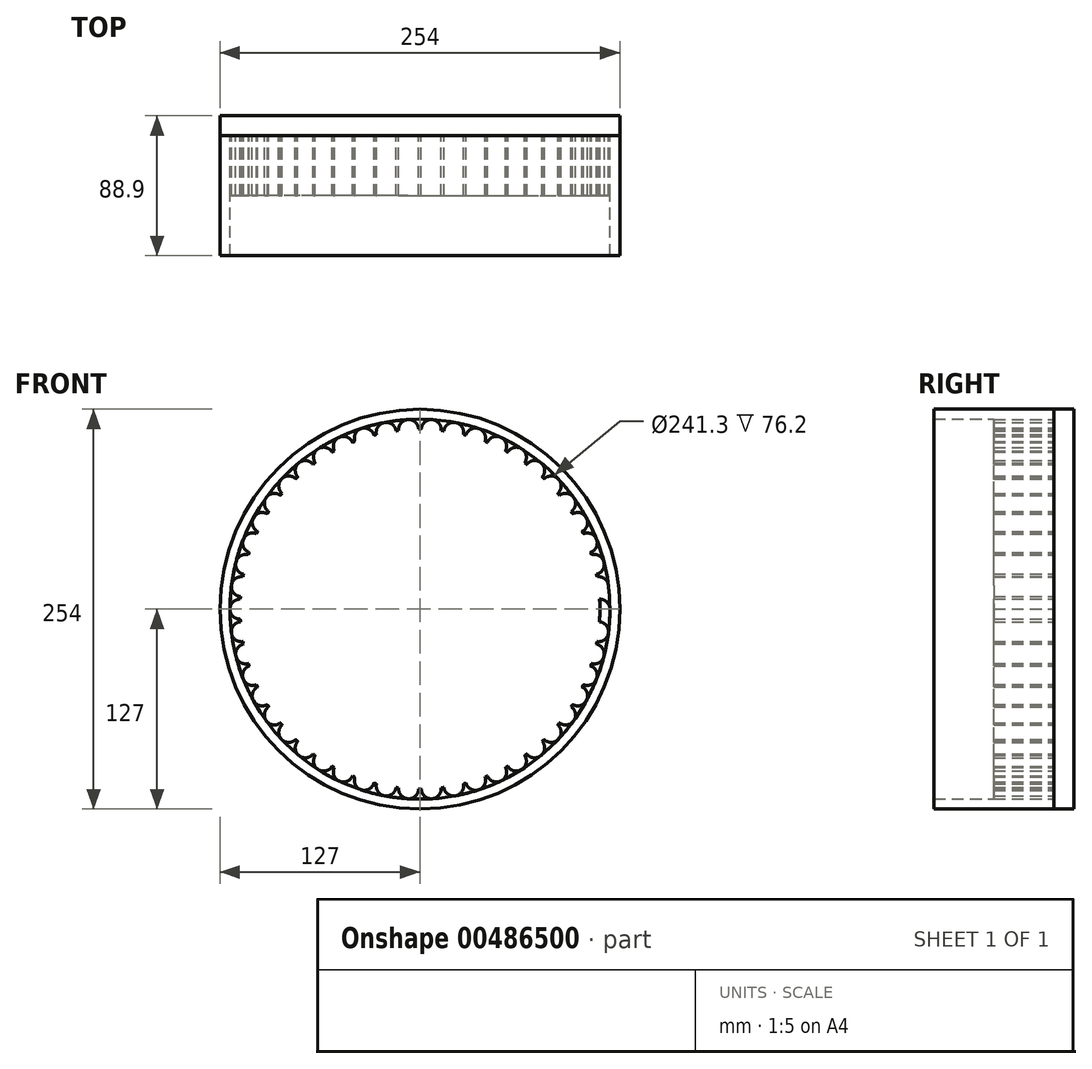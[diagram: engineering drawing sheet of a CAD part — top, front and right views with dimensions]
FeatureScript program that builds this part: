
annotation { "Feature Type Name" : "Feature", "Feature Type Description" : "" }
export const myFeature = defineFeature(function(context is Context, id is Id, definition is map)
    precondition{}
    {
        {
            var Q0;
            Q0=qCreatedBy(makeId("Front.planeOp"),FACE);
            var sketch = newSketch(context, id + "F0", { "sketchPlane" : qUnion([Q0])});
            skCircle(sketch, "E0", {"center": v(0, 0) * mm, "radius": 4.4 * mm});
            skCircle(sketch, "E1", {"center": v(0, 0) * mm, "radius": 127 * mm});
            skCircle(sketch, "E2", {"center": v(0, 0) * mm, "radius": 114.3 * mm});
            skCircle(sketch, "E3", {"center": v(0, 0) * mm, "radius": 120.65 * mm});
            skLineSegment(sketch, "E4", {"start": v(-114.3, 0) * mm, "end": v(114.3, 0) * mm});
            skLineSegment(sketch, "E5", {"start": v(0, -114.3) * mm, "end": v(0, 114.3) * mm});
            skCircle(sketch, "E6", {"center": v(-114.3, 0) * mm, "radius": 6.35 * mm});
            skCircle(sketch, "E7.1.0", {"center": v(-113.4, -14.33) * mm, "radius": 6.35 * mm});
            skCircle(sketch, "E7.2.0", {"center": v(-110.7, -28.43) * mm, "radius": 6.35 * mm});
            skCircle(sketch, "E7.3.0", {"center": v(-106.27, -42.08) * mm, "radius": 6.35 * mm});
            skCircle(sketch, "E7.4.0", {"center": v(-100.16, -55.06) * mm, "radius": 6.35 * mm});
            skCircle(sketch, "E7.5.0", {"center": v(-92.47, -67.18) * mm, "radius": 6.35 * mm});
            skCircle(sketch, "E7.6.0", {"center": v(-83.32, -78.24) * mm, "radius": 6.35 * mm});
            skCircle(sketch, "E7.7.0", {"center": v(-72.86, -88.07) * mm, "radius": 6.35 * mm});
            skCircle(sketch, "E7.8.0", {"center": v(-61.25, -96.5) * mm, "radius": 6.35 * mm});
            skCircle(sketch, "E7.9.0", {"center": v(-48.67, -103.42) * mm, "radius": 6.35 * mm});
            skCircle(sketch, "E7.10.0", {"center": v(-35.32, -108.7) * mm, "radius": 6.35 * mm});
            skCircle(sketch, "E7.11.0", {"center": v(-21.42, -112.28) * mm, "radius": 6.35 * mm});
            skCircle(sketch, "E7.12.0", {"center": v(-7.18, -114.07) * mm, "radius": 6.35 * mm});
            skCircle(sketch, "E7.13.0", {"center": v(7.18, -114.07) * mm, "radius": 6.35 * mm});
            skCircle(sketch, "E7.14.0", {"center": v(21.42, -112.28) * mm, "radius": 6.35 * mm});
            skCircle(sketch, "E7.15.0", {"center": v(35.32, -108.7) * mm, "radius": 6.35 * mm});
            skCircle(sketch, "E7.16.0", {"center": v(48.67, -103.42) * mm, "radius": 6.35 * mm});
            skCircle(sketch, "E7.17.0", {"center": v(61.25, -96.5) * mm, "radius": 6.35 * mm});
            skCircle(sketch, "E7.18.0", {"center": v(72.86, -88.07) * mm, "radius": 6.35 * mm});
            skCircle(sketch, "E7.19.0", {"center": v(83.32, -78.24) * mm, "radius": 6.35 * mm});
            skCircle(sketch, "E7.20.0", {"center": v(92.47, -67.18) * mm, "radius": 6.35 * mm});
            skCircle(sketch, "E7.21.0", {"center": v(100.16, -55.06) * mm, "radius": 6.35 * mm});
            skCircle(sketch, "E7.22.0", {"center": v(106.27, -42.08) * mm, "radius": 6.35 * mm});
            skCircle(sketch, "E7.23.0", {"center": v(110.7, -28.43) * mm, "radius": 6.35 * mm});
            skCircle(sketch, "E7.24.0", {"center": v(113.4, -14.33) * mm, "radius": 6.35 * mm});
            skCircle(sketch, "E7.25.0", {"center": v(114.3, 0) * mm, "radius": 6.35 * mm});
            skCircle(sketch, "E7.26.0", {"center": v(113.4, 14.33) * mm, "radius": 6.35 * mm});
            skCircle(sketch, "E7.27.0", {"center": v(110.7, 28.43) * mm, "radius": 6.35 * mm});
            skCircle(sketch, "E7.28.0", {"center": v(106.27, 42.08) * mm, "radius": 6.35 * mm});
            skCircle(sketch, "E7.29.0", {"center": v(100.16, 55.06) * mm, "radius": 6.35 * mm});
            skCircle(sketch, "E7.30.0", {"center": v(92.47, 67.18) * mm, "radius": 6.35 * mm});
            skCircle(sketch, "E7.31.0", {"center": v(83.32, 78.24) * mm, "radius": 6.35 * mm});
            skCircle(sketch, "E7.32.0", {"center": v(72.86, 88.07) * mm, "radius": 6.35 * mm});
            skCircle(sketch, "E7.33.0", {"center": v(61.25, 96.5) * mm, "radius": 6.35 * mm});
            skCircle(sketch, "E7.34.0", {"center": v(48.67, 103.42) * mm, "radius": 6.35 * mm});
            skCircle(sketch, "E7.35.0", {"center": v(35.32, 108.7) * mm, "radius": 6.35 * mm});
            skCircle(sketch, "E7.36.0", {"center": v(21.42, 112.28) * mm, "radius": 6.35 * mm});
            skCircle(sketch, "E7.37.0", {"center": v(7.18, 114.07) * mm, "radius": 6.35 * mm});
            skCircle(sketch, "E7.38.0", {"center": v(-7.18, 114.07) * mm, "radius": 6.35 * mm});
            skCircle(sketch, "E7.39.0", {"center": v(-21.42, 112.28) * mm, "radius": 6.35 * mm});
            skCircle(sketch, "E7.40.0", {"center": v(-35.32, 108.7) * mm, "radius": 6.35 * mm});
            skCircle(sketch, "E7.41.0", {"center": v(-48.67, 103.42) * mm, "radius": 6.35 * mm});
            skCircle(sketch, "E7.42.0", {"center": v(-61.25, 96.5) * mm, "radius": 6.35 * mm});
            skCircle(sketch, "E7.43.0", {"center": v(-72.86, 88.07) * mm, "radius": 6.35 * mm});
            skCircle(sketch, "E7.44.0", {"center": v(-83.32, 78.24) * mm, "radius": 6.35 * mm});
            skCircle(sketch, "E7.45.0", {"center": v(-92.47, 67.18) * mm, "radius": 6.35 * mm});
            skCircle(sketch, "E7.46.0", {"center": v(-100.16, 55.06) * mm, "radius": 6.35 * mm});
            skCircle(sketch, "E7.47.0", {"center": v(-106.27, 42.08) * mm, "radius": 6.35 * mm});
            skCircle(sketch, "E7.48.0", {"center": v(-110.7, 28.43) * mm, "radius": 6.35 * mm});
            skCircle(sketch, "E7.49.0", {"center": v(-113.4, 14.33) * mm, "radius": 6.35 * mm});
            skSolve(sketch);
        }
        {
            var Q0;
            Q0=makeQuery(id+"F0.imprint","IMPRINT",FACE,{"disambiguationData":[TD([[makeQuery(id+"F0.imprint","IMPRINT",EDGE,{"derivedFrom":sQuery(id+"F0.wireOp",EDGE,"E1")}),1.0]])]});
            extrude(context, id + "F1", {"entities" : qUnion([Q0]), "depth" : 76.2 * mm});
        }
        {
            var Q0;
            {var subQ0=sQuery(id+"F0.wireOp",EDGE,"E7.3.0");var subQ1=sQuery(id+"F0.wireOp",EDGE,"E2");var subQ2=makeQuery(id+"F0.imprint","INTERSECT",VERTEX,{"disambiguationData":[OD(1.0)],"derivedFrom":[subQ1,subQ0]});Q0=makeQuery(id+"F0.imprint","IMPRINT",FACE,{"disambiguationData":[TD([[makeQuery(id+"F0.imprint","IMPRINT",EDGE,{"disambiguationData":[TD([[subQ2,-1.0]])],"derivedFrom":subQ1}),-1.0]])]});}
            var Q1;
            {var subQ0=sQuery(id+"F0.wireOp",EDGE,"E7.2.0");var subQ1=sQuery(id+"F0.wireOp",EDGE,"E2");var subQ2=makeQuery(id+"F0.imprint","INTERSECT",VERTEX,{"disambiguationData":[OD(1.0)],"derivedFrom":[subQ1,subQ0]});Q1=makeQuery(id+"F0.imprint","IMPRINT",FACE,{"disambiguationData":[TD([[makeQuery(id+"F0.imprint","IMPRINT",EDGE,{"disambiguationData":[TD([[subQ2,-1.0]])],"derivedFrom":subQ1}),-1.0]])]});}
            var Q2;
            {var subQ0=sQuery(id+"F0.wireOp",EDGE,"E7.1.0");var subQ1=sQuery(id+"F0.wireOp",EDGE,"E2");var subQ2=makeQuery(id+"F0.imprint","INTERSECT",VERTEX,{"disambiguationData":[OD(1.0)],"derivedFrom":[subQ1,subQ0]});Q2=makeQuery(id+"F0.imprint","IMPRINT",FACE,{"disambiguationData":[TD([[makeQuery(id+"F0.imprint","IMPRINT",EDGE,{"disambiguationData":[TD([[subQ2,-1.0]])],"derivedFrom":subQ1}),-1.0]])]});}
            var Q3;
            {var subQ0=sQuery(id+"F0.wireOp",EDGE,"E6");var subQ1=sQuery(id+"F0.wireOp",EDGE,"E2");var subQ2=makeQuery(id+"F0.imprint","INTERSECT",VERTEX,{"disambiguationData":[OD(1.0)],"derivedFrom":[subQ1,subQ0]});Q3=makeQuery(id+"F0.imprint","IMPRINT",FACE,{"disambiguationData":[TD([[makeQuery(id+"F0.imprint","IMPRINT",EDGE,{"disambiguationData":[TD([[subQ2,-1.0]])],"derivedFrom":subQ1}),-1.0]])]});}
            var Q4;
            {var subQ0=sQuery(id+"F0.wireOp",EDGE,"E7.49.0");var subQ1=sQuery(id+"F0.wireOp",EDGE,"E2");var subQ2=makeQuery(id+"F0.imprint","INTERSECT",VERTEX,{"disambiguationData":[OD(1.0)],"derivedFrom":[subQ1,subQ0]});Q4=makeQuery(id+"F0.imprint","IMPRINT",FACE,{"disambiguationData":[TD([[makeQuery(id+"F0.imprint","IMPRINT",EDGE,{"disambiguationData":[TD([[subQ2,-1.0]])],"derivedFrom":subQ1}),-1.0]])]});}
            var Q5;
            {var subQ0=sQuery(id+"F0.wireOp",EDGE,"E7.48.0");var subQ1=sQuery(id+"F0.wireOp",EDGE,"E2");var subQ2=makeQuery(id+"F0.imprint","INTERSECT",VERTEX,{"disambiguationData":[OD(1.0)],"derivedFrom":[subQ1,subQ0]});Q5=makeQuery(id+"F0.imprint","IMPRINT",FACE,{"disambiguationData":[TD([[makeQuery(id+"F0.imprint","IMPRINT",EDGE,{"disambiguationData":[TD([[subQ2,-1.0]])],"derivedFrom":subQ1}),-1.0]])]});}
            var Q6;
            {var subQ0=sQuery(id+"F0.wireOp",EDGE,"E7.47.0");var subQ1=sQuery(id+"F0.wireOp",EDGE,"E2");var subQ2=makeQuery(id+"F0.imprint","INTERSECT",VERTEX,{"disambiguationData":[OD(1.0)],"derivedFrom":[subQ1,subQ0]});Q6=makeQuery(id+"F0.imprint","IMPRINT",FACE,{"disambiguationData":[TD([[makeQuery(id+"F0.imprint","IMPRINT",EDGE,{"disambiguationData":[TD([[subQ2,-1.0]])],"derivedFrom":subQ1}),-1.0]])]});}
            var Q7;
            {var subQ0=sQuery(id+"F0.wireOp",EDGE,"E7.46.0");var subQ1=sQuery(id+"F0.wireOp",EDGE,"E2");var subQ2=makeQuery(id+"F0.imprint","INTERSECT",VERTEX,{"disambiguationData":[OD(1.0)],"derivedFrom":[subQ1,subQ0]});Q7=makeQuery(id+"F0.imprint","IMPRINT",FACE,{"disambiguationData":[TD([[makeQuery(id+"F0.imprint","IMPRINT",EDGE,{"disambiguationData":[TD([[subQ2,-1.0]])],"derivedFrom":subQ1}),-1.0]])]});}
            var Q8;
            {var subQ0=sQuery(id+"F0.wireOp",EDGE,"E7.45.0");var subQ1=sQuery(id+"F0.wireOp",EDGE,"E2");var subQ2=makeQuery(id+"F0.imprint","INTERSECT",VERTEX,{"disambiguationData":[OD(1.0)],"derivedFrom":[subQ1,subQ0]});Q8=makeQuery(id+"F0.imprint","IMPRINT",FACE,{"disambiguationData":[TD([[makeQuery(id+"F0.imprint","IMPRINT",EDGE,{"disambiguationData":[TD([[subQ2,-1.0]])],"derivedFrom":subQ1}),-1.0]])]});}
            var Q9;
            {var subQ0=sQuery(id+"F0.wireOp",EDGE,"E7.44.0");var subQ1=sQuery(id+"F0.wireOp",EDGE,"E2");var subQ2=makeQuery(id+"F0.imprint","INTERSECT",VERTEX,{"disambiguationData":[OD(1.0)],"derivedFrom":[subQ1,subQ0]});Q9=makeQuery(id+"F0.imprint","IMPRINT",FACE,{"disambiguationData":[TD([[makeQuery(id+"F0.imprint","IMPRINT",EDGE,{"disambiguationData":[TD([[subQ2,-1.0]])],"derivedFrom":subQ1}),-1.0]])]});}
            var Q10;
            {var subQ0=sQuery(id+"F0.wireOp",EDGE,"E7.43.0");var subQ1=sQuery(id+"F0.wireOp",EDGE,"E2");var subQ2=makeQuery(id+"F0.imprint","INTERSECT",VERTEX,{"disambiguationData":[OD(1.0)],"derivedFrom":[subQ1,subQ0]});Q10=makeQuery(id+"F0.imprint","IMPRINT",FACE,{"disambiguationData":[TD([[makeQuery(id+"F0.imprint","IMPRINT",EDGE,{"disambiguationData":[TD([[subQ2,-1.0]])],"derivedFrom":subQ1}),-1.0]])]});}
            var Q11;
            {var subQ0=sQuery(id+"F0.wireOp",EDGE,"E7.42.0");var subQ1=sQuery(id+"F0.wireOp",EDGE,"E2");var subQ2=makeQuery(id+"F0.imprint","INTERSECT",VERTEX,{"disambiguationData":[OD(1.0)],"derivedFrom":[subQ1,subQ0]});Q11=makeQuery(id+"F0.imprint","IMPRINT",FACE,{"disambiguationData":[TD([[makeQuery(id+"F0.imprint","IMPRINT",EDGE,{"disambiguationData":[TD([[subQ2,-1.0]])],"derivedFrom":subQ1}),-1.0]])]});}
            var Q12;
            {var subQ0=sQuery(id+"F0.wireOp",EDGE,"E7.41.0");var subQ1=sQuery(id+"F0.wireOp",EDGE,"E2");var subQ2=makeQuery(id+"F0.imprint","INTERSECT",VERTEX,{"disambiguationData":[OD(1.0)],"derivedFrom":[subQ1,subQ0]});Q12=makeQuery(id+"F0.imprint","IMPRINT",FACE,{"disambiguationData":[TD([[makeQuery(id+"F0.imprint","IMPRINT",EDGE,{"disambiguationData":[TD([[subQ2,-1.0]])],"derivedFrom":subQ1}),-1.0]])]});}
            var Q13;
            {var subQ0=sQuery(id+"F0.wireOp",EDGE,"E7.40.0");var subQ1=sQuery(id+"F0.wireOp",EDGE,"E2");var subQ2=makeQuery(id+"F0.imprint","INTERSECT",VERTEX,{"disambiguationData":[OD(1.0)],"derivedFrom":[subQ1,subQ0]});Q13=makeQuery(id+"F0.imprint","IMPRINT",FACE,{"disambiguationData":[TD([[makeQuery(id+"F0.imprint","IMPRINT",EDGE,{"disambiguationData":[TD([[subQ2,-1.0]])],"derivedFrom":subQ1}),-1.0]])]});}
            var Q14;
            {var subQ0=sQuery(id+"F0.wireOp",EDGE,"E7.39.0");var subQ1=sQuery(id+"F0.wireOp",EDGE,"E2");var subQ2=makeQuery(id+"F0.imprint","INTERSECT",VERTEX,{"disambiguationData":[OD(1.0)],"derivedFrom":[subQ1,subQ0]});Q14=makeQuery(id+"F0.imprint","IMPRINT",FACE,{"disambiguationData":[TD([[makeQuery(id+"F0.imprint","IMPRINT",EDGE,{"disambiguationData":[TD([[subQ2,-1.0]])],"derivedFrom":subQ1}),-1.0]])]});}
            var Q15;
            {var subQ0=sQuery(id+"F0.wireOp",EDGE,"E7.38.0");var subQ1=sQuery(id+"F0.wireOp",EDGE,"E2");var subQ2=makeQuery(id+"F0.imprint","INTERSECT",VERTEX,{"disambiguationData":[OD(1.0)],"derivedFrom":[subQ1,subQ0]});Q15=makeQuery(id+"F0.imprint","IMPRINT",FACE,{"disambiguationData":[TD([[makeQuery(id+"F0.imprint","IMPRINT",EDGE,{"disambiguationData":[TD([[subQ2,-1.0]])],"derivedFrom":subQ1}),-1.0]])]});}
            var Q16;
            {var subQ1=sQuery(id+"F0.wireOp",EDGE,"E2");var subQ5=makeQuery(id+"F0.imprint","INTERSECT",VERTEX,{"disambiguationData":[OD(1.0)],"derivedFrom":[subQ1,sQuery(id+"F0.wireOp",EDGE,"E5")]});Q16=makeQuery(id+"F0.imprint","IMPRINT",FACE,{"disambiguationData":[TD([[makeQuery(id+"F0.imprint","IMPRINT",EDGE,{"disambiguationData":[TD([[subQ5,1.0]])],"derivedFrom":subQ1}),-1.0]])]});}
            var Q17;
            {var subQ0=sQuery(id+"F0.wireOp",EDGE,"E7.36.0");var subQ1=sQuery(id+"F0.wireOp",EDGE,"E2");var subQ2=makeQuery(id+"F0.imprint","INTERSECT",VERTEX,{"disambiguationData":[OD(1.0)],"derivedFrom":[subQ1,subQ0]});Q17=makeQuery(id+"F0.imprint","IMPRINT",FACE,{"disambiguationData":[TD([[makeQuery(id+"F0.imprint","IMPRINT",EDGE,{"disambiguationData":[TD([[subQ2,-1.0]])],"derivedFrom":subQ1}),-1.0]])]});}
            var Q18;
            {var subQ0=sQuery(id+"F0.wireOp",EDGE,"E7.35.0");var subQ1=sQuery(id+"F0.wireOp",EDGE,"E2");var subQ2=makeQuery(id+"F0.imprint","INTERSECT",VERTEX,{"disambiguationData":[OD(1.0)],"derivedFrom":[subQ1,subQ0]});Q18=makeQuery(id+"F0.imprint","IMPRINT",FACE,{"disambiguationData":[TD([[makeQuery(id+"F0.imprint","IMPRINT",EDGE,{"disambiguationData":[TD([[subQ2,-1.0]])],"derivedFrom":subQ1}),-1.0]])]});}
            var Q19;
            {var subQ0=sQuery(id+"F0.wireOp",EDGE,"E7.34.0");var subQ1=sQuery(id+"F0.wireOp",EDGE,"E2");var subQ2=makeQuery(id+"F0.imprint","INTERSECT",VERTEX,{"disambiguationData":[OD(1.0)],"derivedFrom":[subQ1,subQ0]});Q19=makeQuery(id+"F0.imprint","IMPRINT",FACE,{"disambiguationData":[TD([[makeQuery(id+"F0.imprint","IMPRINT",EDGE,{"disambiguationData":[TD([[subQ2,-1.0]])],"derivedFrom":subQ1}),-1.0]])]});}
            var Q20;
            {var subQ0=sQuery(id+"F0.wireOp",EDGE,"E7.33.0");var subQ1=sQuery(id+"F0.wireOp",EDGE,"E2");var subQ2=makeQuery(id+"F0.imprint","INTERSECT",VERTEX,{"disambiguationData":[OD(1.0)],"derivedFrom":[subQ1,subQ0]});Q20=makeQuery(id+"F0.imprint","IMPRINT",FACE,{"disambiguationData":[TD([[makeQuery(id+"F0.imprint","IMPRINT",EDGE,{"disambiguationData":[TD([[subQ2,-1.0]])],"derivedFrom":subQ1}),-1.0]])]});}
            var Q21;
            {var subQ0=sQuery(id+"F0.wireOp",EDGE,"E7.32.0");var subQ1=sQuery(id+"F0.wireOp",EDGE,"E2");var subQ2=makeQuery(id+"F0.imprint","INTERSECT",VERTEX,{"disambiguationData":[OD(1.0)],"derivedFrom":[subQ1,subQ0]});Q21=makeQuery(id+"F0.imprint","IMPRINT",FACE,{"disambiguationData":[TD([[makeQuery(id+"F0.imprint","IMPRINT",EDGE,{"disambiguationData":[TD([[subQ2,-1.0]])],"derivedFrom":subQ1}),-1.0]])]});}
            var Q22;
            {var subQ0=sQuery(id+"F0.wireOp",EDGE,"E7.31.0");var subQ1=sQuery(id+"F0.wireOp",EDGE,"E2");var subQ2=makeQuery(id+"F0.imprint","INTERSECT",VERTEX,{"disambiguationData":[OD(1.0)],"derivedFrom":[subQ1,subQ0]});Q22=makeQuery(id+"F0.imprint","IMPRINT",FACE,{"disambiguationData":[TD([[makeQuery(id+"F0.imprint","IMPRINT",EDGE,{"disambiguationData":[TD([[subQ2,-1.0]])],"derivedFrom":subQ1}),-1.0]])]});}
            var Q23;
            {var subQ0=sQuery(id+"F0.wireOp",EDGE,"E7.30.0");var subQ1=sQuery(id+"F0.wireOp",EDGE,"E2");var subQ2=makeQuery(id+"F0.imprint","INTERSECT",VERTEX,{"disambiguationData":[OD(1.0)],"derivedFrom":[subQ1,subQ0]});Q23=makeQuery(id+"F0.imprint","IMPRINT",FACE,{"disambiguationData":[TD([[makeQuery(id+"F0.imprint","IMPRINT",EDGE,{"disambiguationData":[TD([[subQ2,-1.0]])],"derivedFrom":subQ1}),-1.0]])]});}
            var Q24;
            {var subQ0=sQuery(id+"F0.wireOp",EDGE,"E7.29.0");var subQ1=sQuery(id+"F0.wireOp",EDGE,"E2");var subQ2=makeQuery(id+"F0.imprint","INTERSECT",VERTEX,{"disambiguationData":[OD(1.0)],"derivedFrom":[subQ1,subQ0]});Q24=makeQuery(id+"F0.imprint","IMPRINT",FACE,{"disambiguationData":[TD([[makeQuery(id+"F0.imprint","IMPRINT",EDGE,{"disambiguationData":[TD([[subQ2,-1.0]])],"derivedFrom":subQ1}),-1.0]])]});}
            var Q25;
            {var subQ0=sQuery(id+"F0.wireOp",EDGE,"E7.28.0");var subQ1=sQuery(id+"F0.wireOp",EDGE,"E2");var subQ2=makeQuery(id+"F0.imprint","INTERSECT",VERTEX,{"disambiguationData":[OD(1.0)],"derivedFrom":[subQ1,subQ0]});Q25=makeQuery(id+"F0.imprint","IMPRINT",FACE,{"disambiguationData":[TD([[makeQuery(id+"F0.imprint","IMPRINT",EDGE,{"disambiguationData":[TD([[subQ2,-1.0]])],"derivedFrom":subQ1}),-1.0]])]});}
            var Q26;
            {var subQ0=sQuery(id+"F0.wireOp",EDGE,"E7.27.0");var subQ1=sQuery(id+"F0.wireOp",EDGE,"E2");var subQ2=makeQuery(id+"F0.imprint","INTERSECT",VERTEX,{"disambiguationData":[OD(1.0)],"derivedFrom":[subQ1,subQ0]});Q26=makeQuery(id+"F0.imprint","IMPRINT",FACE,{"disambiguationData":[TD([[makeQuery(id+"F0.imprint","IMPRINT",EDGE,{"disambiguationData":[TD([[subQ2,-1.0]])],"derivedFrom":subQ1}),-1.0]])]});}
            var Q27;
            {var subQ0=sQuery(id+"F0.wireOp",EDGE,"E7.26.0");var subQ1=sQuery(id+"F0.wireOp",EDGE,"E2");var subQ2=makeQuery(id+"F0.imprint","INTERSECT",VERTEX,{"disambiguationData":[OD(1.0)],"derivedFrom":[subQ1,subQ0]});Q27=makeQuery(id+"F0.imprint","IMPRINT",FACE,{"disambiguationData":[TD([[makeQuery(id+"F0.imprint","IMPRINT",EDGE,{"disambiguationData":[TD([[subQ2,-1.0]])],"derivedFrom":subQ1}),-1.0]])]});}
            var Q28;
            {var subQ0=sQuery(id+"F0.wireOp",EDGE,"E7.25.0");var subQ1=sQuery(id+"F0.wireOp",EDGE,"E2");var subQ2=makeQuery(id+"F0.imprint","INTERSECT",VERTEX,{"disambiguationData":[OD(0.0)],"derivedFrom":[subQ1,subQ0]});Q28=makeQuery(id+"F0.imprint","IMPRINT",FACE,{"disambiguationData":[TD([[makeQuery(id+"F0.imprint","IMPRINT",EDGE,{"disambiguationData":[TD([[subQ2,-1.0]])],"derivedFrom":subQ1}),-1.0]])]});}
            var Q29;
            {var subQ0=sQuery(id+"F0.wireOp",EDGE,"E7.24.0");var subQ1=sQuery(id+"F0.wireOp",EDGE,"E2");var subQ2=makeQuery(id+"F0.imprint","INTERSECT",VERTEX,{"disambiguationData":[OD(1.0)],"derivedFrom":[subQ1,subQ0]});Q29=makeQuery(id+"F0.imprint","IMPRINT",FACE,{"disambiguationData":[TD([[makeQuery(id+"F0.imprint","IMPRINT",EDGE,{"disambiguationData":[TD([[subQ2,-1.0]])],"derivedFrom":subQ1}),-1.0]])]});}
            var Q30;
            {var subQ0=sQuery(id+"F0.wireOp",EDGE,"E7.23.0");var subQ1=sQuery(id+"F0.wireOp",EDGE,"E2");var subQ2=makeQuery(id+"F0.imprint","INTERSECT",VERTEX,{"disambiguationData":[OD(1.0)],"derivedFrom":[subQ1,subQ0]});Q30=makeQuery(id+"F0.imprint","IMPRINT",FACE,{"disambiguationData":[TD([[makeQuery(id+"F0.imprint","IMPRINT",EDGE,{"disambiguationData":[TD([[subQ2,-1.0]])],"derivedFrom":subQ1}),-1.0]])]});}
            var Q31;
            {var subQ0=sQuery(id+"F0.wireOp",EDGE,"E7.22.0");var subQ1=sQuery(id+"F0.wireOp",EDGE,"E2");var subQ2=makeQuery(id+"F0.imprint","INTERSECT",VERTEX,{"disambiguationData":[OD(1.0)],"derivedFrom":[subQ1,subQ0]});Q31=makeQuery(id+"F0.imprint","IMPRINT",FACE,{"disambiguationData":[TD([[makeQuery(id+"F0.imprint","IMPRINT",EDGE,{"disambiguationData":[TD([[subQ2,-1.0]])],"derivedFrom":subQ1}),-1.0]])]});}
            var Q32;
            {var subQ0=sQuery(id+"F0.wireOp",EDGE,"E7.21.0");var subQ1=sQuery(id+"F0.wireOp",EDGE,"E2");var subQ2=makeQuery(id+"F0.imprint","INTERSECT",VERTEX,{"disambiguationData":[OD(1.0)],"derivedFrom":[subQ1,subQ0]});Q32=makeQuery(id+"F0.imprint","IMPRINT",FACE,{"disambiguationData":[TD([[makeQuery(id+"F0.imprint","IMPRINT",EDGE,{"disambiguationData":[TD([[subQ2,-1.0]])],"derivedFrom":subQ1}),-1.0]])]});}
            var Q33;
            {var subQ0=sQuery(id+"F0.wireOp",EDGE,"E7.20.0");var subQ1=sQuery(id+"F0.wireOp",EDGE,"E2");var subQ2=makeQuery(id+"F0.imprint","INTERSECT",VERTEX,{"disambiguationData":[OD(1.0)],"derivedFrom":[subQ1,subQ0]});Q33=makeQuery(id+"F0.imprint","IMPRINT",FACE,{"disambiguationData":[TD([[makeQuery(id+"F0.imprint","IMPRINT",EDGE,{"disambiguationData":[TD([[subQ2,-1.0]])],"derivedFrom":subQ1}),-1.0]])]});}
            var Q34;
            {var subQ0=sQuery(id+"F0.wireOp",EDGE,"E7.19.0");var subQ1=sQuery(id+"F0.wireOp",EDGE,"E2");var subQ2=makeQuery(id+"F0.imprint","INTERSECT",VERTEX,{"disambiguationData":[OD(1.0)],"derivedFrom":[subQ1,subQ0]});Q34=makeQuery(id+"F0.imprint","IMPRINT",FACE,{"disambiguationData":[TD([[makeQuery(id+"F0.imprint","IMPRINT",EDGE,{"disambiguationData":[TD([[subQ2,-1.0]])],"derivedFrom":subQ1}),-1.0]])]});}
            var Q35;
            {var subQ0=sQuery(id+"F0.wireOp",EDGE,"E7.18.0");var subQ1=sQuery(id+"F0.wireOp",EDGE,"E2");var subQ2=makeQuery(id+"F0.imprint","INTERSECT",VERTEX,{"disambiguationData":[OD(1.0)],"derivedFrom":[subQ1,subQ0]});Q35=makeQuery(id+"F0.imprint","IMPRINT",FACE,{"disambiguationData":[TD([[makeQuery(id+"F0.imprint","IMPRINT",EDGE,{"disambiguationData":[TD([[subQ2,-1.0]])],"derivedFrom":subQ1}),-1.0]])]});}
            var Q36;
            {var subQ0=sQuery(id+"F0.wireOp",EDGE,"E7.17.0");var subQ1=sQuery(id+"F0.wireOp",EDGE,"E2");var subQ2=makeQuery(id+"F0.imprint","INTERSECT",VERTEX,{"disambiguationData":[OD(1.0)],"derivedFrom":[subQ1,subQ0]});Q36=makeQuery(id+"F0.imprint","IMPRINT",FACE,{"disambiguationData":[TD([[makeQuery(id+"F0.imprint","IMPRINT",EDGE,{"disambiguationData":[TD([[subQ2,-1.0]])],"derivedFrom":subQ1}),-1.0]])]});}
            var Q37;
            {var subQ0=sQuery(id+"F0.wireOp",EDGE,"E7.16.0");var subQ1=sQuery(id+"F0.wireOp",EDGE,"E2");var subQ2=makeQuery(id+"F0.imprint","INTERSECT",VERTEX,{"disambiguationData":[OD(1.0)],"derivedFrom":[subQ1,subQ0]});Q37=makeQuery(id+"F0.imprint","IMPRINT",FACE,{"disambiguationData":[TD([[makeQuery(id+"F0.imprint","IMPRINT",EDGE,{"disambiguationData":[TD([[subQ2,-1.0]])],"derivedFrom":subQ1}),-1.0]])]});}
            var Q38;
            {var subQ0=sQuery(id+"F0.wireOp",EDGE,"E7.15.0");var subQ1=sQuery(id+"F0.wireOp",EDGE,"E2");var subQ2=makeQuery(id+"F0.imprint","INTERSECT",VERTEX,{"disambiguationData":[OD(1.0)],"derivedFrom":[subQ1,subQ0]});Q38=makeQuery(id+"F0.imprint","IMPRINT",FACE,{"disambiguationData":[TD([[makeQuery(id+"F0.imprint","IMPRINT",EDGE,{"disambiguationData":[TD([[subQ2,-1.0]])],"derivedFrom":subQ1}),-1.0]])]});}
            var Q39;
            {var subQ0=sQuery(id+"F0.wireOp",EDGE,"E7.14.0");var subQ1=sQuery(id+"F0.wireOp",EDGE,"E2");var subQ2=makeQuery(id+"F0.imprint","INTERSECT",VERTEX,{"disambiguationData":[OD(1.0)],"derivedFrom":[subQ1,subQ0]});Q39=makeQuery(id+"F0.imprint","IMPRINT",FACE,{"disambiguationData":[TD([[makeQuery(id+"F0.imprint","IMPRINT",EDGE,{"disambiguationData":[TD([[subQ2,-1.0]])],"derivedFrom":subQ1}),-1.0]])]});}
            var Q40;
            {var subQ0=sQuery(id+"F0.wireOp",EDGE,"E7.13.0");var subQ1=sQuery(id+"F0.wireOp",EDGE,"E2");var subQ2=makeQuery(id+"F0.imprint","INTERSECT",VERTEX,{"disambiguationData":[OD(1.0)],"derivedFrom":[subQ1,subQ0]});Q40=makeQuery(id+"F0.imprint","IMPRINT",FACE,{"disambiguationData":[TD([[makeQuery(id+"F0.imprint","IMPRINT",EDGE,{"disambiguationData":[TD([[subQ2,-1.0]])],"derivedFrom":subQ1}),-1.0]])]});}
            var Q41;
            {var subQ5=sQuery(id+"F0.wireOp",EDGE,"E2");var subQ6=makeQuery(id+"F0.imprint","INTERSECT",VERTEX,{"disambiguationData":[OD(0.0)],"derivedFrom":[subQ5,sQuery(id+"F0.wireOp",EDGE,"E5")]});Q41=makeQuery(id+"F0.imprint","IMPRINT",FACE,{"disambiguationData":[TD([[makeQuery(id+"F0.imprint","IMPRINT",EDGE,{"disambiguationData":[TD([[subQ6,1.0]])],"derivedFrom":subQ5}),-1.0]])]});}
            var Q42;
            {var subQ0=sQuery(id+"F0.wireOp",EDGE,"E7.11.0");var subQ1=sQuery(id+"F0.wireOp",EDGE,"E2");var subQ2=makeQuery(id+"F0.imprint","INTERSECT",VERTEX,{"disambiguationData":[OD(1.0)],"derivedFrom":[subQ1,subQ0]});Q42=makeQuery(id+"F0.imprint","IMPRINT",FACE,{"disambiguationData":[TD([[makeQuery(id+"F0.imprint","IMPRINT",EDGE,{"disambiguationData":[TD([[subQ2,-1.0]])],"derivedFrom":subQ1}),-1.0]])]});}
            var Q43;
            {var subQ0=sQuery(id+"F0.wireOp",EDGE,"E7.10.0");var subQ1=sQuery(id+"F0.wireOp",EDGE,"E2");var subQ2=makeQuery(id+"F0.imprint","INTERSECT",VERTEX,{"disambiguationData":[OD(1.0)],"derivedFrom":[subQ1,subQ0]});Q43=makeQuery(id+"F0.imprint","IMPRINT",FACE,{"disambiguationData":[TD([[makeQuery(id+"F0.imprint","IMPRINT",EDGE,{"disambiguationData":[TD([[subQ2,-1.0]])],"derivedFrom":subQ1}),-1.0]])]});}
            var Q44;
            {var subQ0=sQuery(id+"F0.wireOp",EDGE,"E7.9.0");var subQ1=sQuery(id+"F0.wireOp",EDGE,"E2");var subQ2=makeQuery(id+"F0.imprint","INTERSECT",VERTEX,{"disambiguationData":[OD(1.0)],"derivedFrom":[subQ1,subQ0]});Q44=makeQuery(id+"F0.imprint","IMPRINT",FACE,{"disambiguationData":[TD([[makeQuery(id+"F0.imprint","IMPRINT",EDGE,{"disambiguationData":[TD([[subQ2,-1.0]])],"derivedFrom":subQ1}),-1.0]])]});}
            var Q45;
            {var subQ0=sQuery(id+"F0.wireOp",EDGE,"E7.8.0");var subQ1=sQuery(id+"F0.wireOp",EDGE,"E2");var subQ2=makeQuery(id+"F0.imprint","INTERSECT",VERTEX,{"disambiguationData":[OD(1.0)],"derivedFrom":[subQ1,subQ0]});Q45=makeQuery(id+"F0.imprint","IMPRINT",FACE,{"disambiguationData":[TD([[makeQuery(id+"F0.imprint","IMPRINT",EDGE,{"disambiguationData":[TD([[subQ2,-1.0]])],"derivedFrom":subQ1}),-1.0]])]});}
            var Q46;
            {var subQ0=sQuery(id+"F0.wireOp",EDGE,"E7.7.0");var subQ1=sQuery(id+"F0.wireOp",EDGE,"E2");var subQ2=makeQuery(id+"F0.imprint","INTERSECT",VERTEX,{"disambiguationData":[OD(1.0)],"derivedFrom":[subQ1,subQ0]});Q46=makeQuery(id+"F0.imprint","IMPRINT",FACE,{"disambiguationData":[TD([[makeQuery(id+"F0.imprint","IMPRINT",EDGE,{"disambiguationData":[TD([[subQ2,-1.0]])],"derivedFrom":subQ1}),-1.0]])]});}
            var Q47;
            {var subQ0=sQuery(id+"F0.wireOp",EDGE,"E7.6.0");var subQ1=sQuery(id+"F0.wireOp",EDGE,"E2");var subQ2=makeQuery(id+"F0.imprint","INTERSECT",VERTEX,{"disambiguationData":[OD(1.0)],"derivedFrom":[subQ1,subQ0]});Q47=makeQuery(id+"F0.imprint","IMPRINT",FACE,{"disambiguationData":[TD([[makeQuery(id+"F0.imprint","IMPRINT",EDGE,{"disambiguationData":[TD([[subQ2,-1.0]])],"derivedFrom":subQ1}),-1.0]])]});}
            var Q48;
            {var subQ0=sQuery(id+"F0.wireOp",EDGE,"E7.5.0");var subQ1=sQuery(id+"F0.wireOp",EDGE,"E2");var subQ2=makeQuery(id+"F0.imprint","INTERSECT",VERTEX,{"disambiguationData":[OD(1.0)],"derivedFrom":[subQ1,subQ0]});Q48=makeQuery(id+"F0.imprint","IMPRINT",FACE,{"disambiguationData":[TD([[makeQuery(id+"F0.imprint","IMPRINT",EDGE,{"disambiguationData":[TD([[subQ2,-1.0]])],"derivedFrom":subQ1}),-1.0]])]});}
            var Q49;
            {var subQ0=sQuery(id+"F0.wireOp",EDGE,"E7.4.0");var subQ1=sQuery(id+"F0.wireOp",EDGE,"E2");var subQ2=makeQuery(id+"F0.imprint","INTERSECT",VERTEX,{"disambiguationData":[OD(1.0)],"derivedFrom":[subQ1,subQ0]});Q49=makeQuery(id+"F0.imprint","IMPRINT",FACE,{"disambiguationData":[TD([[makeQuery(id+"F0.imprint","IMPRINT",EDGE,{"disambiguationData":[TD([[subQ2,-1.0]])],"derivedFrom":subQ1}),-1.0]])]});}
            extrude(context, id + "F2", {"entities" : qUnion([Q0, Q1, Q2, Q3, Q4, Q5, Q6, Q7, Q8, Q9, Q10, Q11, Q12, Q13, Q14, Q15, Q16, Q17, Q18, Q19, Q20, Q21, Q22, Q23, Q24, Q25, Q26, Q27, Q28, Q29, Q30, Q31, Q32, Q33, Q34, Q35, Q36, Q37, Q38, Q39, Q40, Q41, Q42, Q43, Q44, Q45, Q46, Q47, Q48, Q49]), "operationType" : NewBodyOperationType.ADD, "depth" : 38.1 * mm});
        }
        {
            var Q0;
            Q0=qCreatedBy(makeId("Front.planeOp"),FACE);
            var sketch = newSketch(context, id + "F3", { "sketchPlane" : qUnion([Q0])});
            skCircle(sketch, "E8", {"center": v(0, 0) * mm, "radius": 127 * mm});
            skSolve(sketch);
        }
        {
            var Q0;
            Q0=makeQuery(id+"F3.imprint","IMPRINT",FACE,{"disambiguationData":[TD([[makeQuery(id+"F3.imprint","IMPRINT",EDGE,{"derivedFrom":sQuery(id+"F3.wireOp",EDGE,"E8")}),1.0]])]});
            extrude(context, id + "F4", {"entities" : qUnion([Q0]), "oppositeDirection" : true, "depth" : 12.7 * mm});
        }
    });
